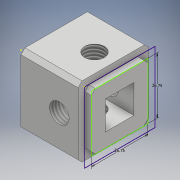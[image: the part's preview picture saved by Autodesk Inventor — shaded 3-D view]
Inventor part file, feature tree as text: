
AUTODESK INVENTOR PART (.ipt)
format: ipt  version: 2017 (Build 210142000, 142)  size: 169,984 bytes
history: native  units: mm
features: sketch x9, extrude x6, thread x5, chamfer x1
ambient origin geometry x8: Origin, YZ Plane, XZ Plane, XY Plane, X Axis, Y Axis, Z Axis, Center Point
bodies: Solid1 (feature_tree)
feature tree (21):
  extrude  "Extrusion1"  Depth=33.25mm
  sketch  "Sketch2"  dims[d2=30.0mm d3=0.0mm d4=26.75mm]
  sketch  "Sketch3"  dims[d5=26.75mm]
  extrude  "Extrusion2"  Depth=26.75mm
  chamfer  "Chamfer1"  Distance=3.0mm
  extrude  "Extrusion3"  Depth=13.5mm
  sketch  "Sketch6"  dims[d10=1.875mm d11=2.0mm d12=45.0deg d13=13.5mm]
  extrude  "Extrusion4"  Depth=6.625mm
  extrude  "Extrusion5"  Depth=26.75mm TaperAngle=0.0deg
  thread  "Thread1"  [1 undecoded]
  thread  "Thread2"  [1 undecoded]
  thread  "Thread3"  [1 undecoded]
  thread  "Thread4"  [1 undecoded]
  extrude  "Extrusion6"  Depth=10.0mm TaperAngle=0.0deg
  thread  "Thread5"  [1 undecoded]
  sketch  "Sketch1"  dims[d0=33.25mm d1=33.25mm]
  sketch  "Sketch4"  dims[d6=26.75mm]
  sketch  "Sketch5"  dims[d7=26.75mm d8=3.0mm d9=0.0mm]
  sketch  "Sketch7"  dims[d14=13.5mm d15=6.625mm]
  sketch  "Sketch8"  dims[d16=6.625mm d17=26.75mm d18=0.0mm d19=9.25mm d20=33.25mm d21=0.0mm d22=9.25mm d23=33.25mm d24=0.0mm]
  sketch  "Sketch9"  dims[d25=10.0mm d26=0.0mm d27=10.0mm d28=0.0mm d29=10.0mm d30=0.0mm d31=10.0mm d32=0.0mm d33=9.25mm d34=10.0mm d35=0.0mm d36=10.0mm d37=0.0mm]
note: 5 required parameter values undecoded (feature->parameter linkage not recoverable at this tier; creation-order binding heuristic only, values carry confidence <= 0.55)
